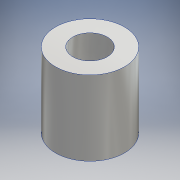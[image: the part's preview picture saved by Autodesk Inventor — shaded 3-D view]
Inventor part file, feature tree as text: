
AUTODESK INVENTOR PART (.ipt)
format: ipt  version: 2020.2 (Build 242310000, 310)  size: 105,472 bytes
history: native  units: mm
features: other x1, extrude x1, sketch x1
ambient origin geometry x8: Origin, YZ Plane, XZ Plane, XY Plane, X Axis, Y Axis, Z Axis, Center Point
bodies: Body1 (feature_tree)
feature tree (3):
  other  "ソリッド1"
  extrude  "押し出し1"  Depth=6.0mm
  sketch  "スケッチ1"
